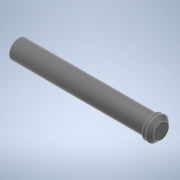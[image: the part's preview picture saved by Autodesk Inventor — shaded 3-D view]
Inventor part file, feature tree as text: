
AUTODESK INVENTOR PART (.ipt)
format: ipt  version: 2021 (Build 250183000, 183)  size: 112,640 bytes
history: native  units: mm
features: extrude x3, sketch x3, chamfer x1
ambient origin geometry x8: Origin, YZ Plane, XZ Plane, XY Plane, X Axis, Y Axis, Z Axis, Center Point
bodies: Solid1 (feature_tree)
feature tree (7):
  extrude  "Extrusion1"  Depth=20.0mm TaperAngle=0.0deg
  extrude  "Extrusion2"  Depth=2.0mm TaperAngle=0.0deg
  chamfer  "Chamfer1"  Distance=2.0mm Angle=45.0deg
  extrude  "Extrusion4"  [1 undecoded]
  sketch  "Sketch1"  dims[d0=5.0mm d1=20.0mm d2=0.0mm]
  sketch  "Sketch2"  dims[d3=6.0mm d4=2.0mm d5=0.0mm d6=1.0mm d7=2.0mm d8=45.0deg]
  sketch  "Sketch4"  dims[d14=15.0mm d15=0.0mm]
note: 1 required parameter value undecoded (feature->parameter linkage not recoverable at this tier; creation-order binding heuristic only, values carry confidence <= 0.55)
